# Revit family: Cambio Wall Systems - Art and Graphic - CHEVRON 36x36
name_source: partatom
category: Generic Models
units: mm (PartAtom-declared; Revit-internal decimal feet)

## family parameters
Can host rebar = No
Cut with Voids When Loaded = No
Host = Face
Maintain Annotation Orientation = No
Part Type = Normal
Room Calculation Point = No
Round Connector Dimension = Use Diameter
Shared = No

## types (4) — shared parameters
Default Elevation = 4' - 0"

## per-type parameters (varying)
| type | Cambio Material | Cambio Material 2 |
| Art and Graphics - HONEYCOMB EVENING SHADOW | Cambio Art and Graphics - Honeycomb | Cambio Art and Graphics - Evening Shadow |
| Art and Graphics - PEACOCK PLUME EVENING SHADOW | Cambio Art and Graphics - Peacock Plume | Cambio Art and Graphics - Evening Shadow |
| Art and Graphics - ROCKWOOD JADE | Cambio Art and Graphics - Rockwood Jade | Cambio Art and Graphics - Maple |
| Art and Graphics - SAGUARO WHITE FLOUR | Cambio Art and Graphics - Saguaro | Cambio Art and Graphics - White Flour |
